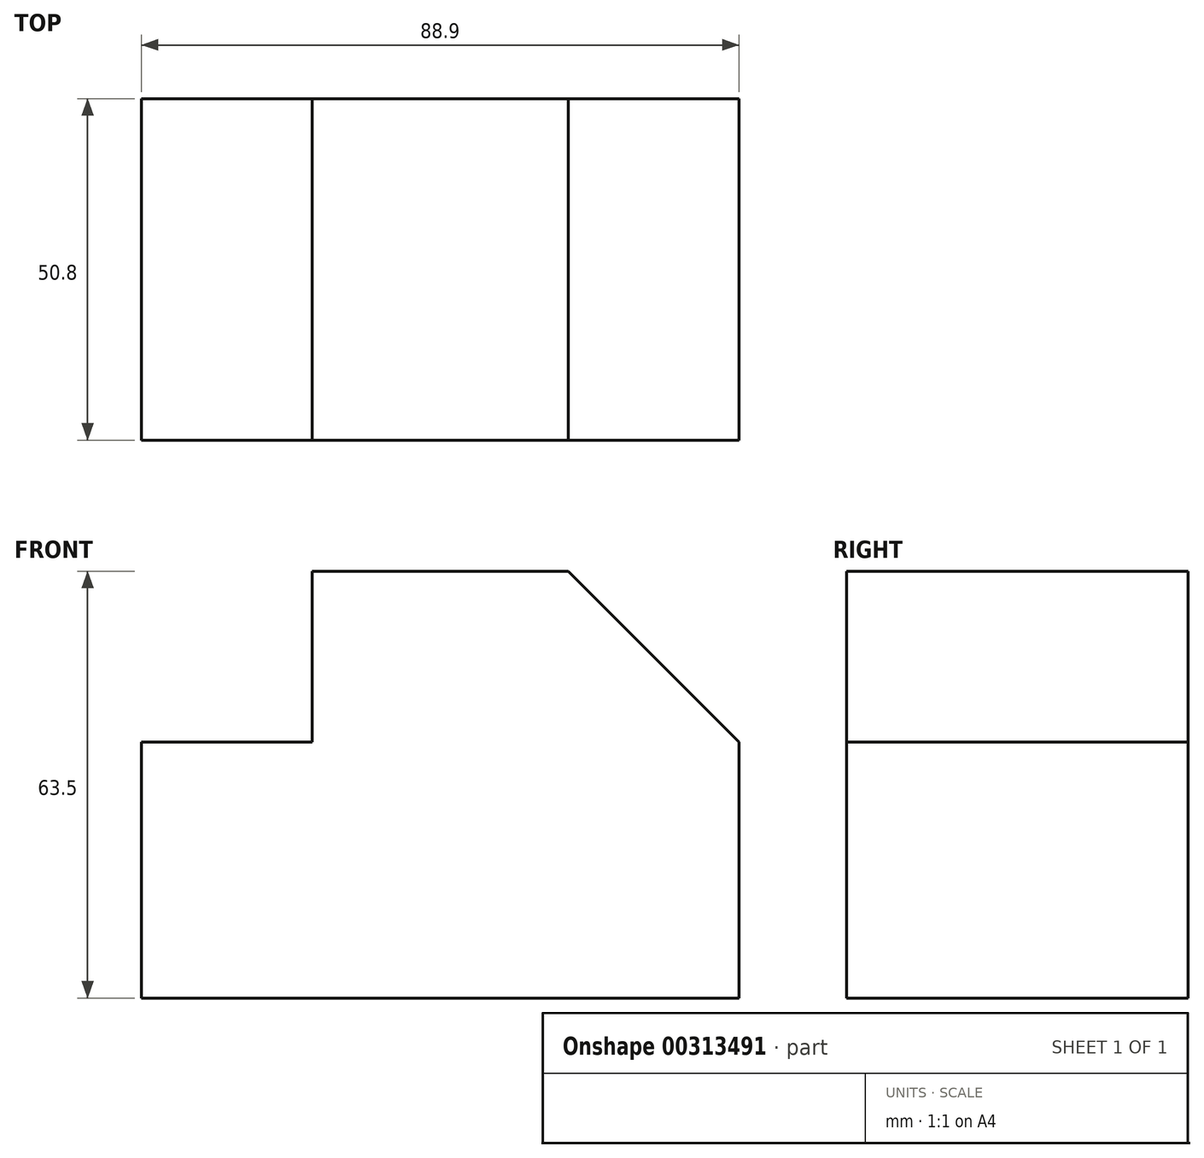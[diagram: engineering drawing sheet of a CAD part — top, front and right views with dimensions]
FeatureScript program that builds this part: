
annotation { "Feature Type Name" : "Feature", "Feature Type Description" : "" }
export const myFeature = defineFeature(function(context is Context, id is Id, definition is map)
    precondition{}
    {
        {
            var Q0;
            Q0=qCreatedBy(makeId("Front.planeOp"),FACE);
            var sketch = newSketch(context, id + "F0", { "sketchPlane" : qUnion([Q0])});
            skLineSegment(sketch, "E0", {"start": v(-44.91, -34.82) * mm, "end": v(43.99, -34.82) * mm});
            skLineSegment(sketch, "E1", {"start": v(-44.91, -34.82) * mm, "end": v(-44.91, 3.28) * mm});
            skLineSegment(sketch, "E2", {"start": v(-44.91, 3.28) * mm, "end": v(-19.51, 3.28) * mm});
            skLineSegment(sketch, "E3", {"start": v(-19.51, 3.28) * mm, "end": v(-19.51, 28.68) * mm});
            skLineSegment(sketch, "E4", {"start": v(-19.51, 28.68) * mm, "end": v(18.59, 28.68) * mm});
            skLineSegment(sketch, "E5", {"start": v(43.99, -34.82) * mm, "end": v(43.99, 3.28) * mm});
            skLineSegment(sketch, "E6", {"start": v(18.59, 28.68) * mm, "end": v(43.99, 3.28) * mm});
            skSolve(sketch);
        }
        {
            var Q0;
            Q0 = qSketchRegion(id + "F0", true);
            extrude(context, id + "F1", {"entities" : qUnion([Q0]), "oppositeDirection" : true, "depth" : 50.8 * mm});
        }
    });
